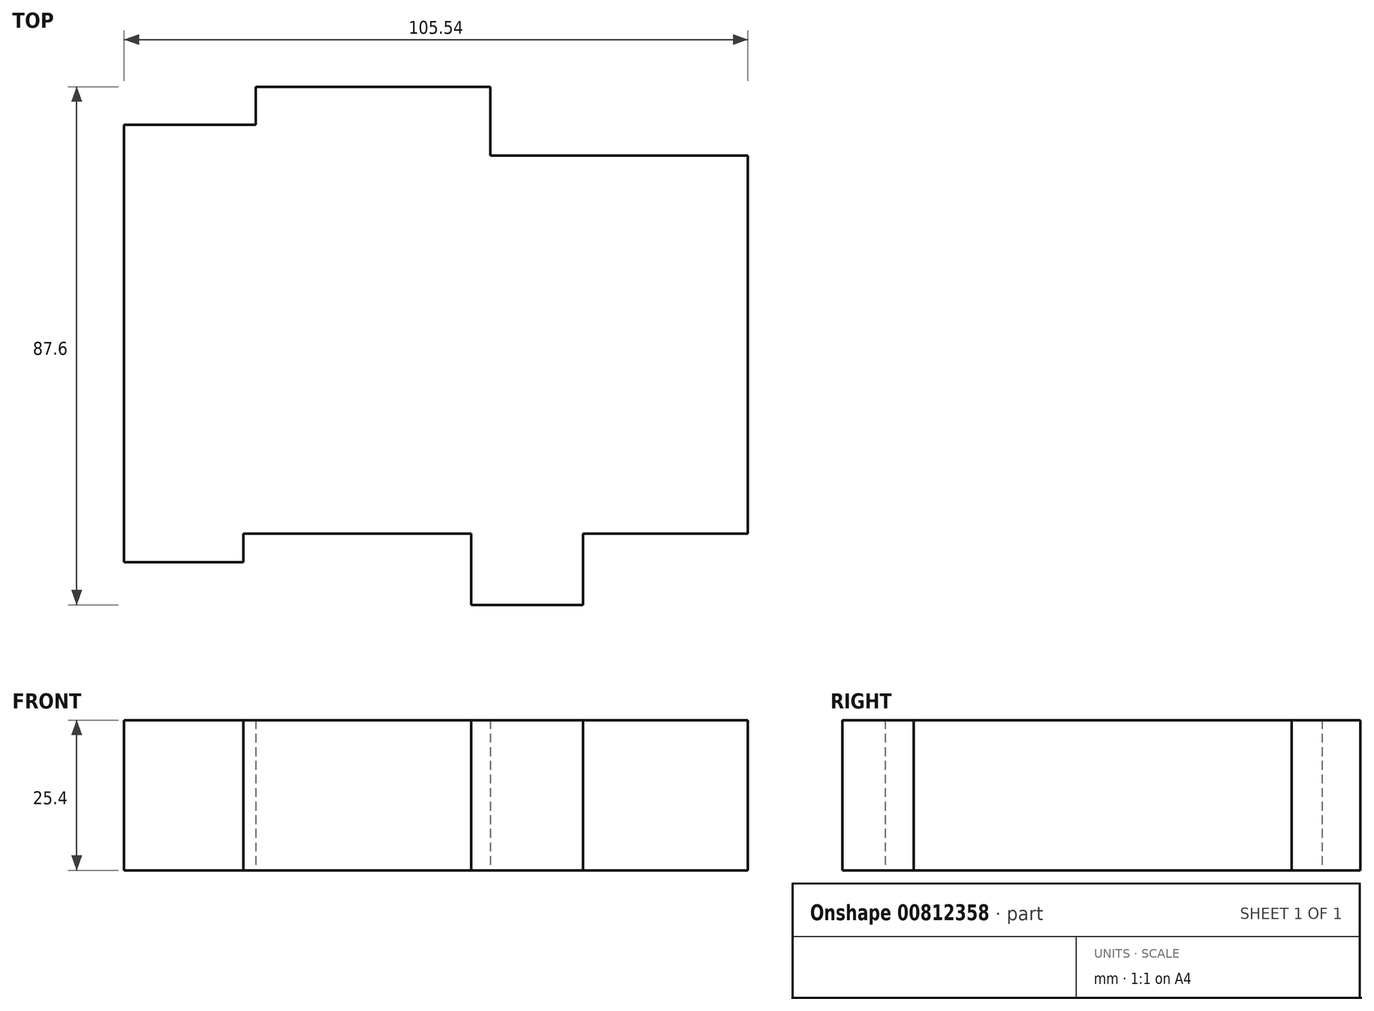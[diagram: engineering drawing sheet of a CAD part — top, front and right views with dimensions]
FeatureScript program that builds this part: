
annotation { "Feature Type Name" : "Feature", "Feature Type Description" : "" }
export const myFeature = defineFeature(function(context is Context, id is Id, definition is map)
    precondition{}
    {
        {
            var Q0;
            Q0=qCreatedBy(makeId("Top.planeOp"),FACE);
            var sketch = newSketch(context, id + "F0", { "sketchPlane" : qUnion([Q0])});
            skLineSegment(sketch, "E0", {"start": v(-79.87, -6.83) * mm, "end": v(-79.87, 67.1) * mm});
            skLineSegment(sketch, "E1", {"start": v(-79.87, 67.1) * mm, "end": v(-57.61, 67.1) * mm});
            skLineSegment(sketch, "E2", {"start": v(-57.61, 73.54) * mm, "end": v(-57.61, 67.1) * mm});
            skLineSegment(sketch, "E3", {"start": v(-57.61, 73.54) * mm, "end": v(-17.9, 73.54) * mm});
            skLineSegment(sketch, "E4", {"start": v(-17.9, 73.54) * mm, "end": v(-17.9, 61.94) * mm});
            skLineSegment(sketch, "E5", {"start": v(-17.9, 61.94) * mm, "end": v(25.67, 61.94) * mm});
            skLineSegment(sketch, "E6", {"start": v(25.67, 61.85) * mm, "end": v(25.67, 61.94) * mm});
            skLineSegment(sketch, "E7", {"start": v(25.67, -2.03) * mm, "end": v(-2.2, -2.03) * mm});
            skLineSegment(sketch, "E8", {"start": v(-2.2, -2.03) * mm, "end": v(-2.2, -14.06) * mm});
            skLineSegment(sketch, "E9", {"start": v(-2.2, -14.06) * mm, "end": v(-21.13, -14.06) * mm});
            skLineSegment(sketch, "E10", {"start": v(-21.13, -14.06) * mm, "end": v(-21.13, -2) * mm});
            skLineSegment(sketch, "E11", {"start": v(-21.13, -2) * mm, "end": v(-59.7, -2) * mm});
            skLineSegment(sketch, "E12", {"start": v(-59.7, -2) * mm, "end": v(-59.7, -6.83) * mm});
            skLineSegment(sketch, "E13", {"start": v(-59.7, -6.83) * mm, "end": v(-79.87, -6.83) * mm});
            skLineSegment(sketch, "E14", {"start": v(-79.87, -6.83) * mm, "end": v(-79.87, -4.06) * mm});
            skLineSegment(sketch, "E15", {"start": v(25.67, -2.03) * mm, "end": v(25.67, 61.94) * mm});
            skSolve(sketch);
        }
        {
            var Q0;
            Q0 = qSketchRegion(id + "F0", true);
            extrude(context, id + "F1", {"entities" : qUnion([Q0]), "depth" : 25.4 * mm, "offsetDistance" : 25.4 * mm});
        }
    });
